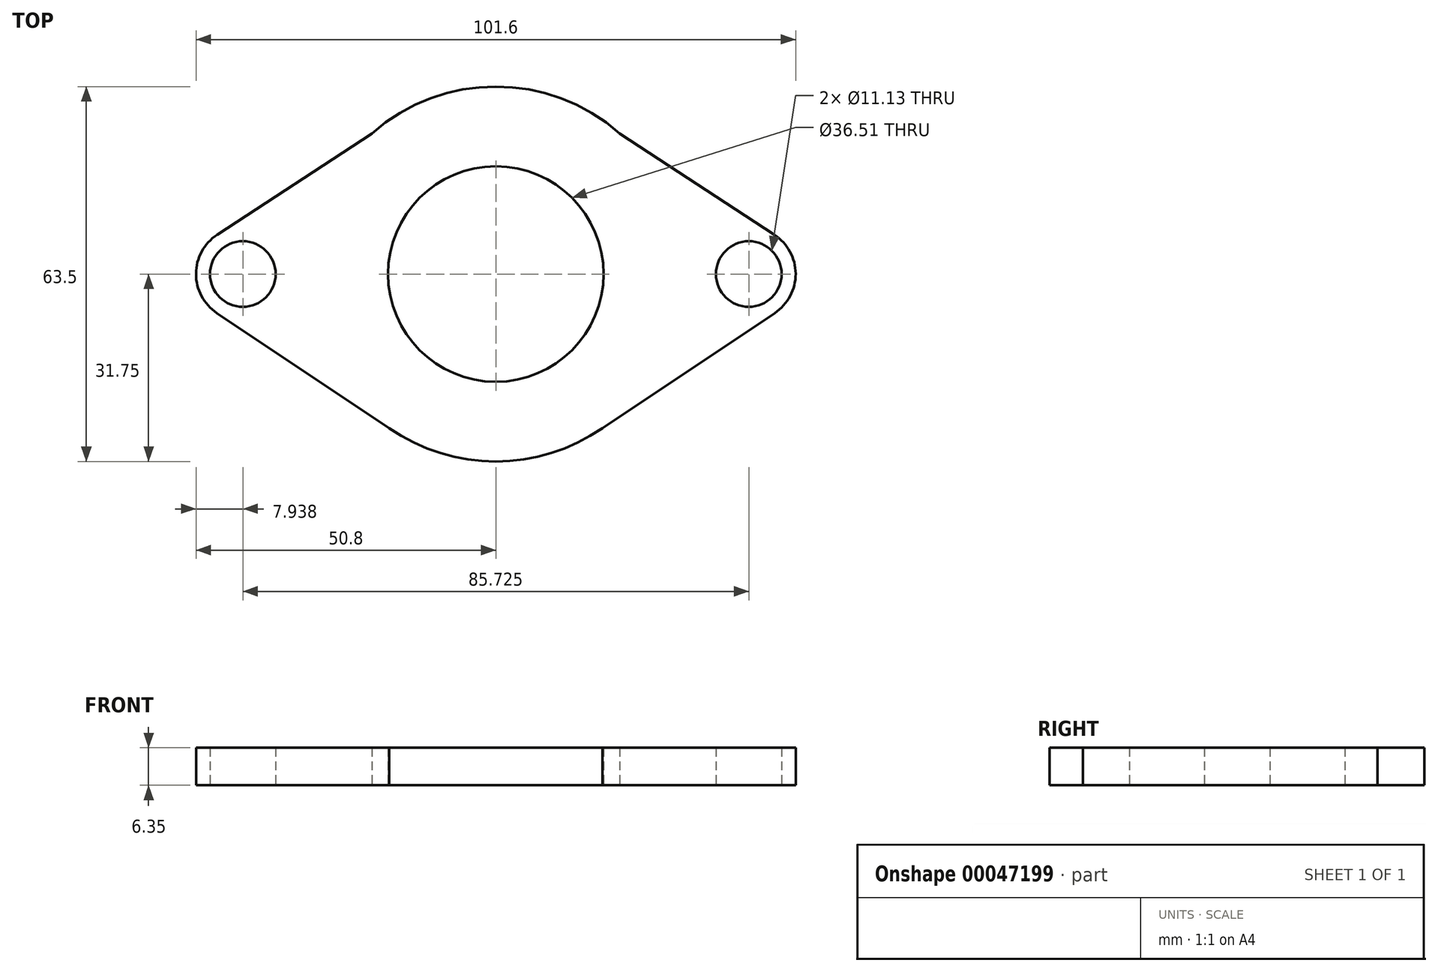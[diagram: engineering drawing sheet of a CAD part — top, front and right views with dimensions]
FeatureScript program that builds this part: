
annotation { "Feature Type Name" : "Feature", "Feature Type Description" : "" }
export const myFeature = defineFeature(function(context is Context, id is Id, definition is map)
    precondition{}
    {
        {
            var Q0;
            Q0=qCreatedBy(makeId("Top.planeOp"),FACE);
            var sketch = newSketch(context, id + "F0", { "sketchPlane" : qUnion([Q0])});
            skCircle(sketch, "E0", {"center": v(0, 0) * mm, "radius": 18.26 * mm});
            skCircle(sketch, "E1", {"center": v(-42.86, 0) * mm, "radius": 5.56 * mm});
            skCircle(sketch, "E2.MirrorC", {"center": v(42.86, 0) * mm, "radius": 5.56 * mm});
            skCircle(sketch, "E3", {"center": v(-42.86, 0) * mm, "radius": 7.94 * mm});
            skCircle(sketch, "E4", {"center": v(0, 0) * mm, "radius": 31.75 * mm});
            skLineSegment(sketch, "E5", {"start": v(-21, 23.8) * mm, "end": v(-47.21, 6.64) * mm});
            skLineSegment(sketch, "E6", {"start": v(-18.08, -26.1) * mm, "end": v(-47.27, -6.6) * mm});
            skLineSegment(sketch, "E7.MirrorCS", {"start": v(21, 23.8) * mm, "end": v(47.21, 6.64) * mm});
            skLineSegment(sketch, "E8.MirrorCS", {"start": v(18.08, -26.1) * mm, "end": v(47.27, -6.6) * mm});
            skCircle(sketch, "E9.MirrorC", {"center": v(42.86, 0) * mm, "radius": 7.94 * mm});
            skSolve(sketch);
        }
        {
            var Q0;
            Q0 = qSketchRegion(id + "F0", true);
            extrude(context, id + "F1", {"entities" : qUnion([Q0]), "depth" : 6.35 * mm});
        }
    });
